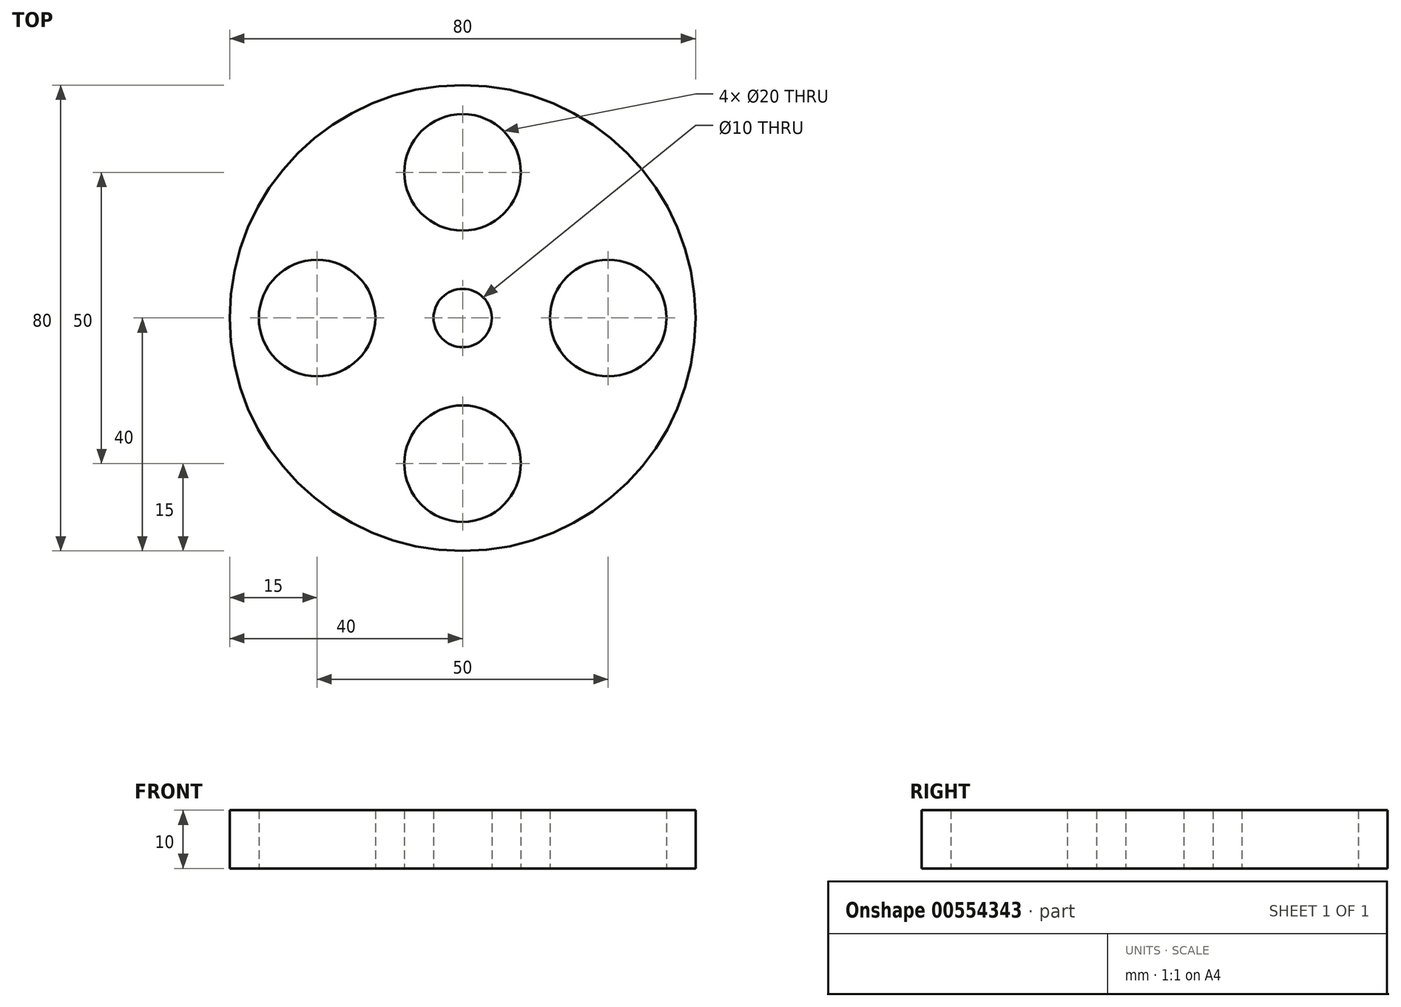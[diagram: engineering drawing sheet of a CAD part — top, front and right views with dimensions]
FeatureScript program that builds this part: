
annotation { "Feature Type Name" : "Feature", "Feature Type Description" : "" }
export const myFeature = defineFeature(function(context is Context, id is Id, definition is map)
    precondition{}
    {
        {
            var Q0;
            Q0=qCreatedBy(makeId("Top.planeOp"),FACE);
            var sketch = newSketch(context, id + "F0", { "sketchPlane" : qUnion([Q0])});
            skCircle(sketch, "E0", {"center": v(0, 0) * mm, "radius": 40 * mm});
            skCircle(sketch, "E1", {"center": v(-25, 0) * mm, "radius": 10 * mm});
            skCircle(sketch, "E2", {"center": v(0, 25) * mm, "radius": 10 * mm});
            skCircle(sketch, "E3", {"center": v(25, 0) * mm, "radius": 10 * mm});
            skCircle(sketch, "E4", {"center": v(0, -25) * mm, "radius": 10 * mm});
            skCircle(sketch, "E5", {"center": v(0, 0) * mm, "radius": 25 * mm, "construction": true});
            skCircle(sketch, "E6", {"center": v(0, 0) * mm, "radius": 5 * mm});
            skSolve(sketch);
        }
        {
            var Q0;
            Q0 = qSketchRegion(id + "F0", true);
            extrude(context, id + "F1", {"entities" : qUnion([Q0]), "depth" : 10 * mm, "offsetDistance" : 25 * mm});
        }
    });
